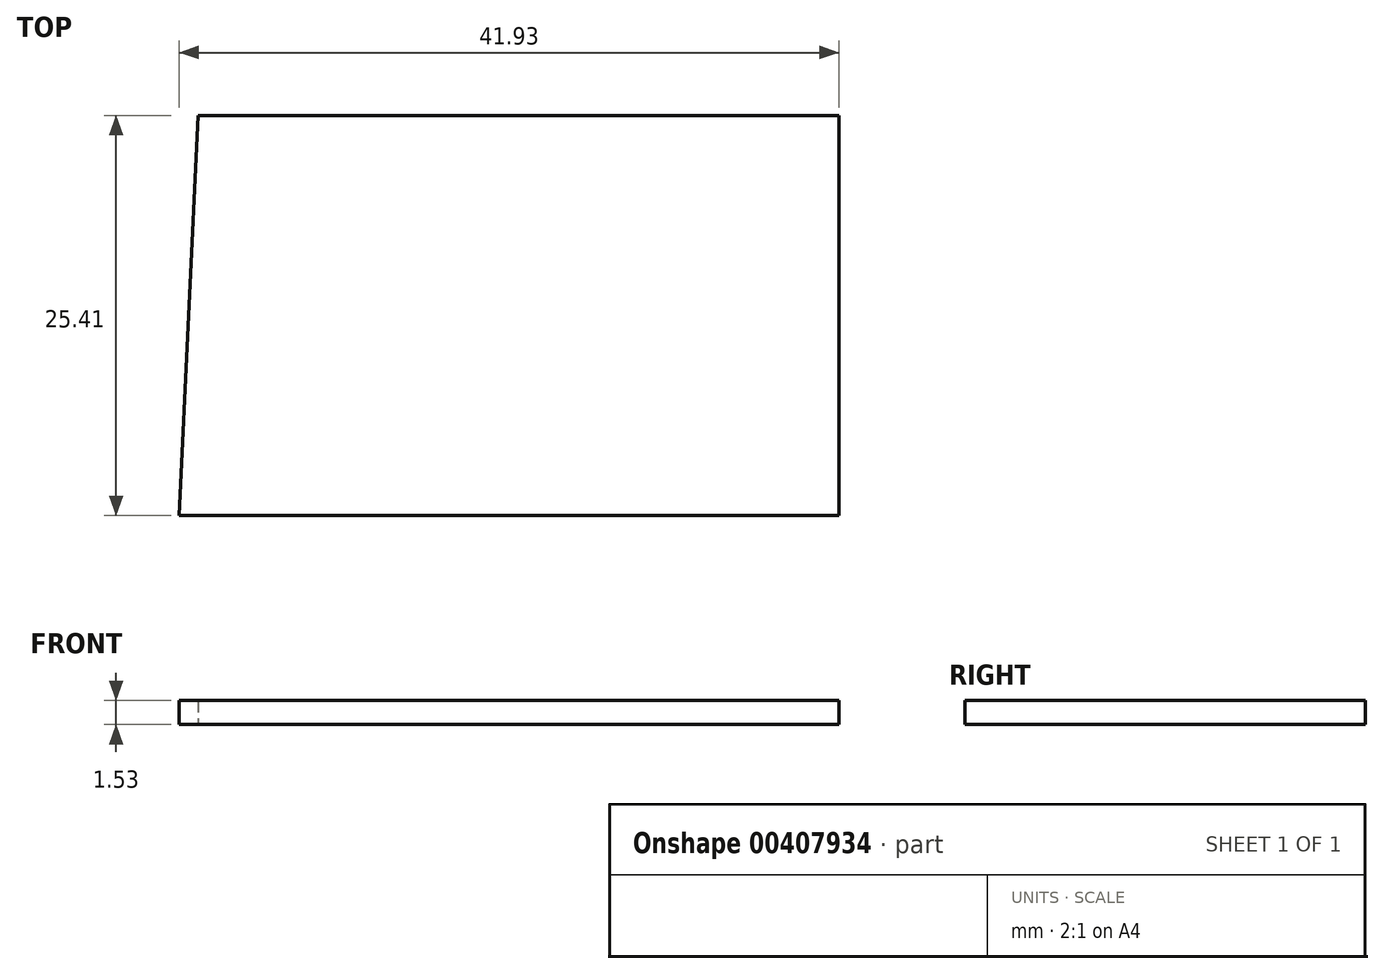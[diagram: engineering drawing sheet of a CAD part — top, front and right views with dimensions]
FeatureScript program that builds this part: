
annotation { "Feature Type Name" : "Feature", "Feature Type Description" : "" }
export const myFeature = defineFeature(function(context is Context, id is Id, definition is map)
    precondition{}
    {
        {
            var Q0;
            Q0=qCreatedBy(makeId("Top.planeOp"),FACE);
            var sketch = newSketch(context, id + "F0", { "sketchPlane" : qUnion([Q0])});
            skLineSegment(sketch, "E0", {"start": v(-28.01, 0) * mm, "end": v(13.92, 0) * mm});
            skLineSegment(sketch, "E1", {"start": v(13.92, 0) * mm, "end": v(13.92, 25.41) * mm});
            skLineSegment(sketch, "E2", {"start": v(13.92, 25.41) * mm, "end": v(-26.78, 25.41) * mm});
            skLineSegment(sketch, "E3", {"start": v(-26.78, 25.41) * mm, "end": v(-28.01, 0) * mm});
            skSolve(sketch);
        }
        {
            var Q0;
            Q0=makeQuery(id+"F0.imprint","IMPRINT",FACE,{"disambiguationData":[TD([[makeQuery(id+"F0.imprint","IMPRINT",EDGE,{"derivedFrom":sQuery(id+"F0.wireOp",EDGE,"E0")}),1.0]])]});
            extrude(context, id + "F1", {"entities" : qUnion([Q0]), "depth" : 1.53 * mm});
        }
    });
